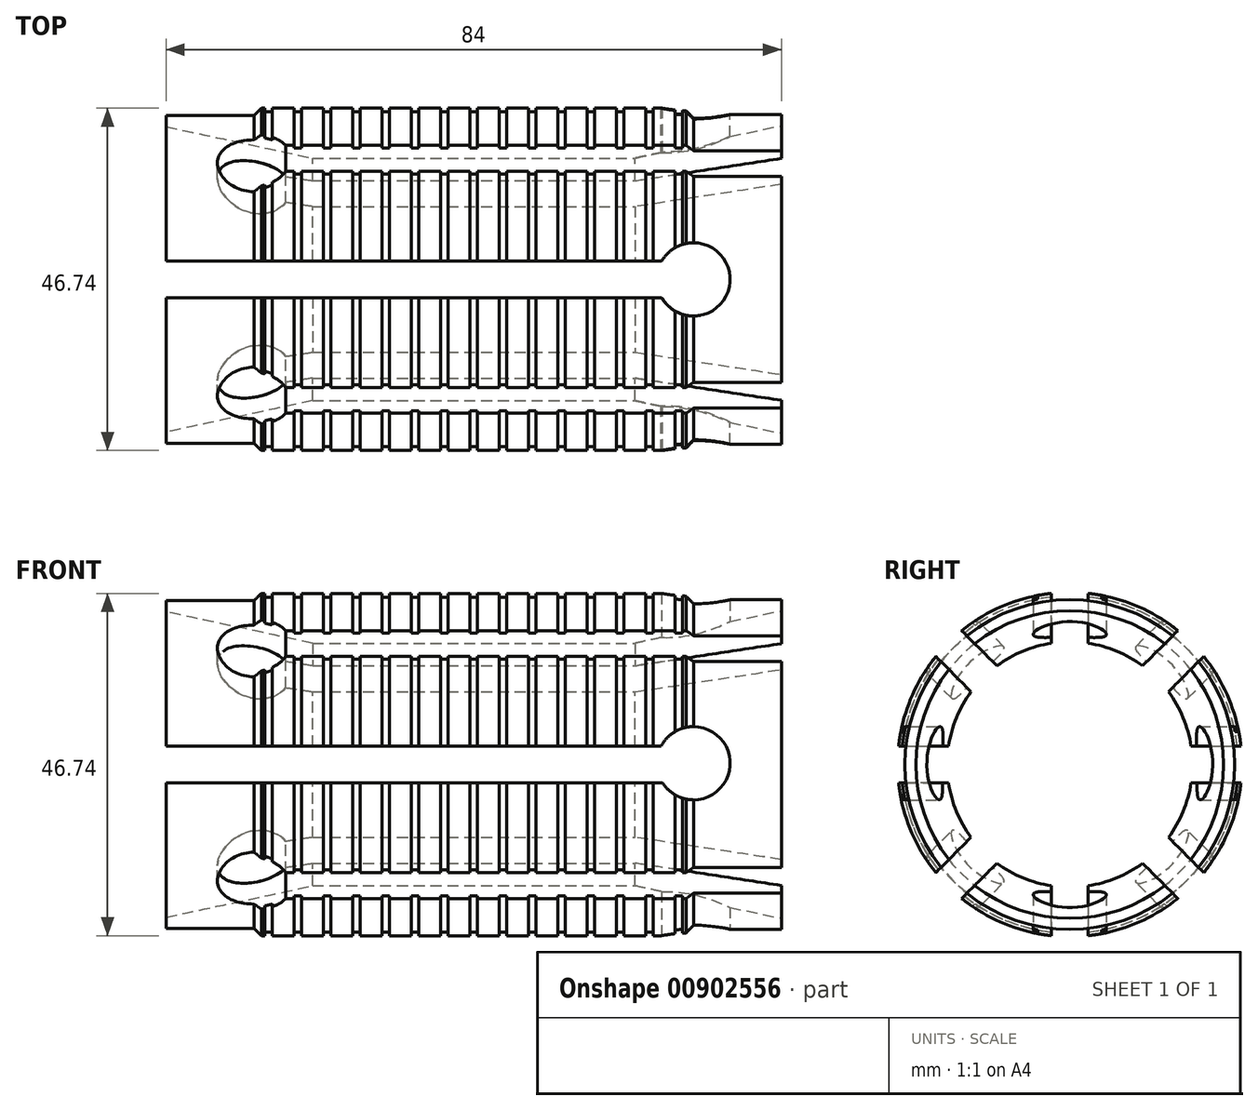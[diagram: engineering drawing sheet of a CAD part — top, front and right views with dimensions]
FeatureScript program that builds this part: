
annotation { "Feature Type Name" : "Feature", "Feature Type Description" : "" }
export const myFeature = defineFeature(function(context is Context, id is Id, definition is map)
    precondition{}
    {
        {
            var Q0;
            Q0=qCreatedBy(makeId("Front.planeOp"),FACE);
            var sketch = newSketch(context, id + "F0", { "sketchPlane" : qUnion([Q0])});
            skLineSegment(sketch, "E0", {"start": v(-42, 22.5) * mm, "end": v(-30, 22.5) * mm});
            skLineSegment(sketch, "E1", {"start": v(-30, 22.5) * mm, "end": v(-30, 23.5) * mm});
            skLineSegment(sketch, "E2", {"start": v(-30, 23.5) * mm, "end": v(0, 23.5) * mm});
            skLineSegment(sketch, "E3", {"start": v(0, 16.75) * mm, "end": v(-22, 16.75) * mm});
            skLineSegment(sketch, "E4", {"start": v(-22, 16.75) * mm, "end": v(-42, 21) * mm});
            skLineSegment(sketch, "E5", {"start": v(-42, 21) * mm, "end": v(-42, 22.5) * mm});
            skLineSegment(sketch, "E6.MirrorCS", {"start": v(30, 23.5) * mm, "end": v(0, 23.5) * mm});
            skLineSegment(sketch, "E7.MirrorCS", {"start": v(42, 22.5) * mm, "end": v(30, 22.5) * mm});
            skLineSegment(sketch, "E8.MirrorCS", {"start": v(22, 16.75) * mm, "end": v(42, 21) * mm});
            skLineSegment(sketch, "E9.MirrorCS", {"start": v(42, 21) * mm, "end": v(42, 22.5) * mm});
            skLineSegment(sketch, "E10.MirrorCS", {"start": v(30, 22.5) * mm, "end": v(30, 23.5) * mm});
            skLineSegment(sketch, "E11.MirrorCS", {"start": v(0, 16.75) * mm, "end": v(22, 16.75) * mm});
            skLineSegment(sketch, "E12", {"start": v(0, 0) * mm, "end": v(-12.65, 0) * mm});
            skLineSegment(sketch, "E13.bottom", {"start": v(28.5, 23.5) * mm, "end": v(27.5, 23.5) * mm});
            skLineSegment(sketch, "E13.top", {"start": v(28.5, 23) * mm, "end": v(27.5, 23) * mm});
            skLineSegment(sketch, "E13.left", {"start": v(28.5, 23.5) * mm, "end": v(28.5, 23) * mm});
            skLineSegment(sketch, "E13.right", {"start": v(27.5, 23.5) * mm, "end": v(27.5, 23) * mm});
            skLineSegment(sketch, "E14.1.0.0", {"start": v(23.5, 23.5) * mm, "end": v(23.5, 23) * mm});
            skLineSegment(sketch, "E14.1.0.1", {"start": v(24.5, 23.5) * mm, "end": v(24.5, 23) * mm});
            skLineSegment(sketch, "E14.1.0.2", {"start": v(24.5, 23) * mm, "end": v(23.5, 23) * mm});
            skLineSegment(sketch, "E14.2.0.0", {"start": v(19.5, 23.5) * mm, "end": v(19.5, 23) * mm});
            skLineSegment(sketch, "E14.2.0.1", {"start": v(20.5, 23.5) * mm, "end": v(20.5, 23) * mm});
            skLineSegment(sketch, "E14.2.0.2", {"start": v(20.5, 23) * mm, "end": v(19.5, 23) * mm});
            skLineSegment(sketch, "E14.3.0.0", {"start": v(15.5, 23.5) * mm, "end": v(15.5, 23) * mm});
            skLineSegment(sketch, "E14.3.0.1", {"start": v(16.5, 23.5) * mm, "end": v(16.5, 23) * mm});
            skLineSegment(sketch, "E14.3.0.2", {"start": v(16.5, 23) * mm, "end": v(15.5, 23) * mm});
            skLineSegment(sketch, "E14.4.0.0", {"start": v(11.5, 23.5) * mm, "end": v(11.5, 23) * mm});
            skLineSegment(sketch, "E14.4.0.1", {"start": v(12.5, 23.5) * mm, "end": v(12.5, 23) * mm});
            skLineSegment(sketch, "E14.4.0.2", {"start": v(12.5, 23) * mm, "end": v(11.5, 23) * mm});
            skLineSegment(sketch, "E14.5.0.0", {"start": v(7.5, 23.5) * mm, "end": v(7.5, 23) * mm});
            skLineSegment(sketch, "E14.5.0.1", {"start": v(8.5, 23.5) * mm, "end": v(8.5, 23) * mm});
            skLineSegment(sketch, "E14.5.0.2", {"start": v(8.5, 23) * mm, "end": v(7.5, 23) * mm});
            skLineSegment(sketch, "E14.6.0.0", {"start": v(3.5, 23.5) * mm, "end": v(3.5, 23) * mm});
            skLineSegment(sketch, "E14.6.0.1", {"start": v(4.5, 23.5) * mm, "end": v(4.5, 23) * mm});
            skLineSegment(sketch, "E14.6.0.2", {"start": v(4.5, 23) * mm, "end": v(3.5, 23) * mm});
            skLineSegment(sketch, "E14.7.0.0", {"start": v(-0.5, 23.5) * mm, "end": v(-0.5, 23) * mm});
            skLineSegment(sketch, "E14.7.0.1", {"start": v(0.5, 23.5) * mm, "end": v(0.5, 23) * mm});
            skLineSegment(sketch, "E14.7.0.2", {"start": v(0.5, 23) * mm, "end": v(-0.5, 23) * mm});
            skLineSegment(sketch, "E14.8.0.0", {"start": v(-4.5, 23.5) * mm, "end": v(-4.5, 23) * mm});
            skLineSegment(sketch, "E14.8.0.1", {"start": v(-3.5, 23.5) * mm, "end": v(-3.5, 23) * mm});
            skLineSegment(sketch, "E14.8.0.2", {"start": v(-3.5, 23) * mm, "end": v(-4.5, 23) * mm});
            skLineSegment(sketch, "E14.9.0.0", {"start": v(-8.5, 23.5) * mm, "end": v(-8.5, 23) * mm});
            skLineSegment(sketch, "E14.9.0.1", {"start": v(-7.5, 23.5) * mm, "end": v(-7.5, 23) * mm});
            skLineSegment(sketch, "E14.9.0.2", {"start": v(-7.5, 23) * mm, "end": v(-8.5, 23) * mm});
            skLineSegment(sketch, "E14.10.0.0", {"start": v(-12.5, 23.5) * mm, "end": v(-12.5, 23) * mm});
            skLineSegment(sketch, "E14.10.0.1", {"start": v(-11.5, 23.5) * mm, "end": v(-11.5, 23) * mm});
            skLineSegment(sketch, "E14.10.0.2", {"start": v(-11.5, 23) * mm, "end": v(-12.5, 23) * mm});
            skLineSegment(sketch, "E14.11.0.0", {"start": v(-16.5, 23.5) * mm, "end": v(-16.5, 23) * mm});
            skLineSegment(sketch, "E14.11.0.1", {"start": v(-15.5, 23.5) * mm, "end": v(-15.5, 23) * mm});
            skLineSegment(sketch, "E14.11.0.2", {"start": v(-15.5, 23) * mm, "end": v(-16.5, 23) * mm});
            skLineSegment(sketch, "E14.12.0.0", {"start": v(-20.5, 23.5) * mm, "end": v(-20.5, 23) * mm});
            skLineSegment(sketch, "E14.12.0.1", {"start": v(-19.5, 23.5) * mm, "end": v(-19.5, 23) * mm});
            skLineSegment(sketch, "E14.12.0.2", {"start": v(-19.5, 23) * mm, "end": v(-20.5, 23) * mm});
            skLineSegment(sketch, "E14.13.0.0", {"start": v(-24.5, 23.5) * mm, "end": v(-24.5, 23) * mm});
            skLineSegment(sketch, "E14.13.0.1", {"start": v(-23.5, 23.5) * mm, "end": v(-23.5, 23) * mm});
            skLineSegment(sketch, "E14.13.0.2", {"start": v(-23.5, 23) * mm, "end": v(-24.5, 23) * mm});
            skLineSegment(sketch, "E14.14.0.0", {"start": v(-28.5, 23.5) * mm, "end": v(-28.5, 23) * mm});
            skLineSegment(sketch, "E14.14.0.1", {"start": v(-27.5, 23.5) * mm, "end": v(-27.5, 23) * mm});
            skLineSegment(sketch, "E14.14.0.2", {"start": v(-27.5, 23) * mm, "end": v(-28.5, 23) * mm});
            skLineSegment(sketch, "E14.direction1", {"start": v(27.5, 23) * mm, "end": v(23.5, 23) * mm, "construction": true});
            skSolve(sketch);
        }
        {
            var Q0;
            Q0=makeQuery(id+"F0.imprint","IMPRINT",FACE,{"disambiguationData":[TD([[makeQuery(id+"F0.imprint","IMPRINT",EDGE,{"derivedFrom":sQuery(id+"F0.wireOp",EDGE,"E0")}),-1.0]])]});
            var Q1;
            Q1=sQuery(id+"F0.wireOp",EDGE,"E12");
            revolve(context, id + "F1", {"surfaceOperationType" : NewSurfaceOperationType.NEW, "entities" : qUnion([Q0]), "axis" : qUnion([Q1]), "revolveType" : RevolveType.FULL});
        }
        {
            var Q0;
            Q0=makeQuery(id+"F1.opRevolve","SWEPT_EDGE",EDGE,{"disambiguationData":[OSD([sQuery(id+"F0.wireOp",EDGE,"E1"),sQuery(id+"F0.wireOp",EDGE,"E2")])]});
            var Q1;
            Q1=makeQuery(id+"F1.opRevolve","SWEPT_EDGE",EDGE,{"disambiguationData":[OSD([sQuery(id+"F0.wireOp",EDGE,"E6.MirrorCS"),sQuery(id+"F0.wireOp",EDGE,"E10.MirrorCS")])]});
            chamfer(context, id + "F2", {"entities" : qUnion([Q0, Q1]), "width" : 1 * mm, "tangentPropagation" : true});
        }
        {
            var Q0;
            Q0=qCreatedBy(makeId("Top.planeOp"),FACE);
            var sketch = newSketch(context, id + "F3", { "sketchPlane" : qUnion([Q0])});
            skArc(sketch, "E15", {"start": v(25.67, -2.5) * mm, "mid": v(35, 0) * mm, "end": v(25.67, 2.5) * mm});
            skLineSegment(sketch, "E16", {"start": v(-43.96, -2.5) * mm, "end": v(25.67, -2.5) * mm});
            skLineSegment(sketch, "E17", {"start": v(25.67, 2.5) * mm, "end": v(-44.34, 2.5) * mm});
            skLineSegment(sketch, "E18", {"start": v(-44.34, 2.5) * mm, "end": v(-44.34, -2.5) * mm});
            skLineSegment(sketch, "E19", {"start": v(-44.34, -2.5) * mm, "end": v(-43.96, -2.5) * mm});
            skSolve(sketch);
        }
        {
            var Q0;
            Q0 = qSketchRegion(id + "F3", true);
            extrude(context, id + "F4", {"entities" : qUnion([Q0]), "operationType" : NewBodyOperationType.REMOVE, "endBound" : BoundingType.SYMMETRIC, "depth" : 50 * mm, "offsetDistance" : 25 * mm});
        }
        {
            var Q0;
            Q0=makeQuery(id+"F4.boolean.opBoolean","INTERSECT",EDGE,{"disambiguationData":[OD(1.0)],"derivedFrom":[makeQuery(id+"F1.opRevolve","SWEPT_FACE",FACE,{"disambiguationData":[OSD([sQuery(id+"F0.wireOp",EDGE,"E3"),sQuery(id+"F0.wireOp",EDGE,"E11.MirrorCS")])]}),makeQuery(id+"F4.opExtrude","SWEPT_FACE",FACE,{"disambiguationData":[OSD([sQuery(id+"F3.wireOp",EDGE,"E17")])]})]});
            cPlane(context, id + "F5", {"entities" : qUnion([Q0]), "cplaneType" : CPlaneType.LINE_ANGLE, "offset" : 25 * mm, "angle" : 45 * degree, "width" : 150 * mm, "height" : 150 * mm});
        }
        {
            var Q0;
            Q0=qCreatedBy(id+"F5.planeOp",FACE);
            var sketch = newSketch(context, id + "F6", { "sketchPlane" : qUnion([Q0])});
            skArc(sketch, "E20", {"start": v(25.67, -2.5) * mm, "mid": v(35, 0) * mm, "end": v(25.67, 2.5) * mm});
            skLineSegment(sketch, "E21", {"start": v(-44.33, -2.5) * mm, "end": v(25.67, -2.5) * mm});
            skLineSegment(sketch, "E22", {"start": v(25.67, 2.5) * mm, "end": v(-44.33, 2.5) * mm});
            skLineSegment(sketch, "E23", {"start": v(-44.33, 2.5) * mm, "end": v(-44.33, -2.5) * mm});
            skSolve(sketch);
        }
        {
            var Q0;
            Q0 = qSketchRegion(id + "F6", true);
            extrude(context, id + "F7", {"entities" : qUnion([Q0]), "operationType" : NewBodyOperationType.REMOVE, "endBound" : BoundingType.SYMMETRIC, "oppositeDirection" : true, "depth" : 80 * mm, "offsetDistance" : 25 * mm});
        }
        {
            var Q0;
            Q0=makeQuery(id+"F7.boolean.opBoolean","INTERSECT",EDGE,{"derivedFrom":[makeQuery(id+"F4.boolean.opBoolean","SPLIT",FACE,{"disambiguationData":[TD([makeQuery(id+"F4.opExtrude","SWEPT_FACE",FACE,{"disambiguationData":[OSD([sQuery(id+"F3.wireOp",EDGE,"E17")])]})])],"derivedFrom":makeQuery(id+"F1.opRevolve","SWEPT_FACE",FACE,{"disambiguationData":[OSD([sQuery(id+"F0.wireOp",EDGE,"E3"),sQuery(id+"F0.wireOp",EDGE,"E11.MirrorCS")])]})}),makeQuery(id+"F7.opExtrude","SWEPT_FACE",FACE,{"disambiguationData":[OSD([sQuery(id+"F6.wireOp",EDGE,"E21")])]})]});
            cPlane(context, id + "F8", {"entities" : qUnion([Q0]), "cplaneType" : CPlaneType.LINE_ANGLE, "offset" : 25 * mm, "angle" : 135 * degree, "width" : 150 * mm, "height" : 150 * mm});
        }
        {
            var Q0;
            Q0=qCreatedBy(makeId("Front.planeOp"),FACE);
            var sketch = newSketch(context, id + "F9", { "sketchPlane" : qUnion([Q0])});
            skArc(sketch, "E24", {"start": v(25.78, -2.5) * mm, "mid": v(35, 0.38) * mm, "end": v(25.57, 2.5) * mm});
            skLineSegment(sketch, "E25", {"start": v(-43.97, -2.5) * mm, "end": v(25.78, -2.5) * mm});
            skLineSegment(sketch, "E26", {"start": v(25.57, 2.5) * mm, "end": v(-44.34, 2.5) * mm});
            skLineSegment(sketch, "E27", {"start": v(-44.34, 2.5) * mm, "end": v(-44.34, -2.5) * mm});
            skLineSegment(sketch, "E28", {"start": v(-44.34, -2.5) * mm, "end": v(-43.97, -2.5) * mm});
            skSolve(sketch);
        }
        {
            var Q0;
            Q0 = qSketchRegion(id + "F9", true);
            extrude(context, id + "F10", {"entities" : qUnion([Q0]), "operationType" : NewBodyOperationType.REMOVE, "endBound" : BoundingType.SYMMETRIC, "depth" : 80 * mm, "offsetDistance" : 25 * mm});
        }
        {
            var Q0;
            Q0=qCreatedBy(id+"F8.planeOp",FACE);
            var sketch = newSketch(context, id + "F11", { "sketchPlane" : qUnion([Q0])});
            skArc(sketch, "E29", {"start": v(-25.67, 2.5) * mm, "mid": v(-35, 0) * mm, "end": v(-25.67, -2.5) * mm});
            skLineSegment(sketch, "E30", {"start": v(43.8, 2.5) * mm, "end": v(-25.67, 2.5) * mm});
            skLineSegment(sketch, "E31", {"start": v(-25.67, -2.5) * mm, "end": v(44.17, -2.5) * mm});
            skLineSegment(sketch, "E32", {"start": v(44.17, -2.5) * mm, "end": v(44.17, 2.5) * mm});
            skLineSegment(sketch, "E33", {"start": v(44.17, 2.5) * mm, "end": v(43.8, 2.5) * mm});
            skSolve(sketch);
        }
        {
            var Q0;
            Q0 = qSketchRegion(id + "F11", true);
            extrude(context, id + "F12", {"entities" : qUnion([Q0]), "operationType" : NewBodyOperationType.REMOVE, "endBound" : BoundingType.SYMMETRIC, "oppositeDirection" : true, "depth" : 80 * mm, "offsetDistance" : 25 * mm});
        }
    });
